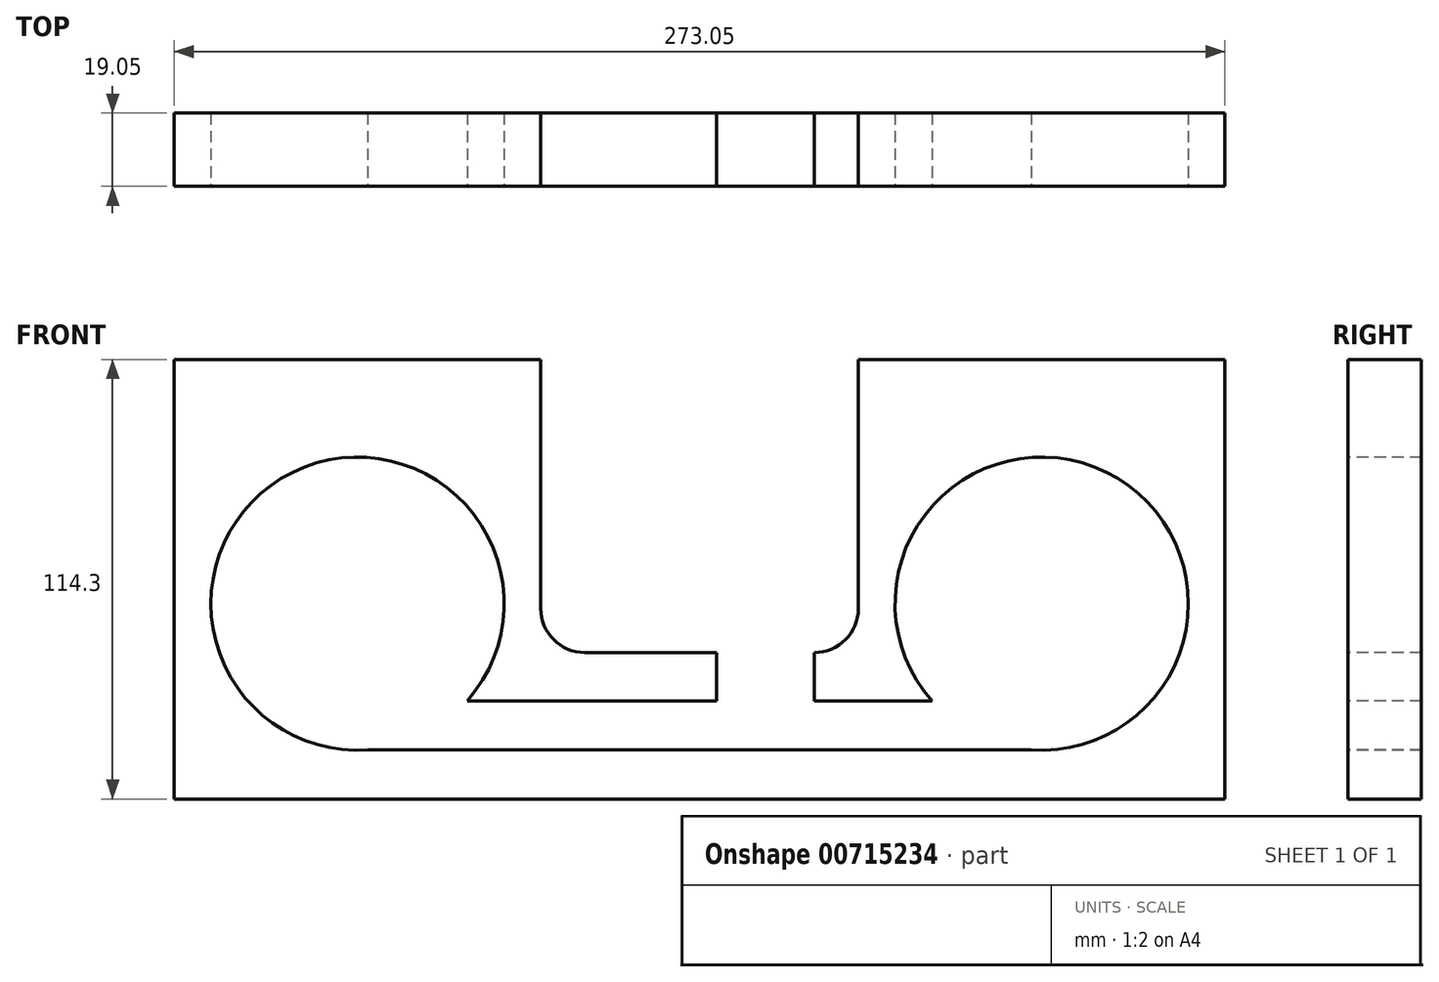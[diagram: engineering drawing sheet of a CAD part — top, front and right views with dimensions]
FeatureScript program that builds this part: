
annotation { "Feature Type Name" : "Feature", "Feature Type Description" : "" }
export const myFeature = defineFeature(function(context is Context, id is Id, definition is map)
    precondition{}
    {
        {
            var Q0;
            Q0=qCreatedBy(makeId("Front.planeOp"),FACE);
            var sketch = newSketch(context, id + "F0", { "sketchPlane" : qUnion([Q0])});
            skLineSegment(sketch, "E0.bottom", {"start": v(0, 0) * mm, "end": v(273.05, 0) * mm});
            skLineSegment(sketch, "E0.top", {"start": v(0, 114.3) * mm, "end": v(273.05, 114.3) * mm});
            skLineSegment(sketch, "E0.left", {"start": v(0, 0) * mm, "end": v(0, 114.3) * mm});
            skLineSegment(sketch, "E0.right", {"start": v(273.05, 0) * mm, "end": v(273.05, 114.3) * mm});
            skSolve(sketch);
        }
        {
            var Q0;
            Q0=makeQuery(id+"F0.imprint","IMPRINT",FACE,{"disambiguationData":[TD([[makeQuery(id+"F0.imprint","IMPRINT",EDGE,{"derivedFrom":sQuery(id+"F0.wireOp",EDGE,"E0.bottom")}),1.0]])]});
            extrude(context, id + "F1", {"entities" : qUnion([Q0]), "depth" : 19.05 * mm, "offsetDistance" : 25.4 * mm});
        }
        {
            var Q0;
            Q0=makeQuery(id+"F1.opExtrude","CAP_FACE",FACE,{"disambiguationData":[OSD([sQuery(id+"F0.wireOp",EDGE,"E0.bottom"),sQuery(id+"F0.wireOp",EDGE,"E0.top"),sQuery(id+"F0.wireOp",EDGE,"E0.left"),sQuery(id+"F0.wireOp",EDGE,"E0.right")])],"isStart":false});
            var sketch = newSketch(context, id + "F2", { "sketchPlane" : qUnion([Q0])});
            skCircle(sketch, "E1", {"center": v(47.63, 50.8) * mm, "radius": 38.1 * mm});
            skCircle(sketch, "E2", {"center": v(225.43, 50.8) * mm, "radius": 38.1 * mm});
            skSolve(sketch);
        }
        {
            var Q0;
            Q0=makeQuery(id+"F2.imprint","IMPRINT",FACE,{"disambiguationData":[TD([[makeQuery(id+"F2.imprint","IMPRINT",EDGE,{"derivedFrom":sQuery(id+"F2.wireOp",EDGE,"E2")}),1.0]])]});
            var Q1;
            Q1=makeQuery(id+"F2.imprint","IMPRINT",FACE,{"disambiguationData":[TD([[makeQuery(id+"F2.imprint","IMPRINT",EDGE,{"derivedFrom":sQuery(id+"F2.wireOp",EDGE,"E1")}),1.0]])]});
            extrude(context, id + "F3", {"entities" : qUnion([Q0, Q1]), "operationType" : NewBodyOperationType.REMOVE, "oppositeDirection" : true, "depth" : 25.4 * mm, "offsetDistance" : 25.4 * mm});
        }
        {
            var Q0;
            Q0=makeQuery(id+"F1.opExtrude","CAP_FACE",FACE,{"disambiguationData":[OSD([sQuery(id+"F0.wireOp",EDGE,"E0.bottom"),sQuery(id+"F0.wireOp",EDGE,"E0.top"),sQuery(id+"F0.wireOp",EDGE,"E0.left"),sQuery(id+"F0.wireOp",EDGE,"E0.right")])],"isStart":false});
            var sketch = newSketch(context, id + "F4", { "sketchPlane" : qUnion([Q0])});
            skLineSegment(sketch, "E3", {"start": v(95.25, 114.3) * mm, "end": v(95.25, 49.53) * mm});
            skLineSegment(sketch, "E4", {"start": v(106.68, 38.1) * mm, "end": v(166.37, 38.1) * mm});
            skLineSegment(sketch, "E5", {"start": v(177.8, 49.53) * mm, "end": v(177.8, 114.3) * mm});
            skPoint(sketch, "E6.visualSharp", {"position": v(95.25, 38.1) * mm});
            skArc(sketch, "E6.filletArc", {"start": v(95.25, 49.53) * mm, "mid": v(98.6, 41.45) * mm, "end": v(106.68, 38.1) * mm});
            skPoint(sketch, "E7.visualSharp", {"position": v(177.8, 38.1) * mm});
            skArc(sketch, "E7.filletArc", {"start": v(166.37, 38.1) * mm, "mid": v(174.45, 41.45) * mm, "end": v(177.8, 49.53) * mm});
            skSolve(sketch);
        }
        {
            var Q0;
            Q0 = qSketchRegion(id + "F4", true);
            var Q1;
            {var subQ1=sQuery(id+"F4.wireOp",EDGE,"E3");Q1=makeQuery(id+"F4.imprint","IMPRINT",FACE,{"disambiguationData":[TD([[makeQuery(id+"F4.imprint","IMPRINT",EDGE,{"derivedFrom":subQ1}),1.0]])]});}
            extrude(context, id + "F5", {"entities" : qUnion([Q0, Q1]), "operationType" : NewBodyOperationType.REMOVE, "oppositeDirection" : true, "depth" : 25.4 * mm, "offsetDistance" : 25.4 * mm});
        }
        {
            var Q0;
            Q0=makeQuery(id+"F1.opExtrude","CAP_FACE",FACE,{"disambiguationData":[OSD([sQuery(id+"F0.wireOp",EDGE,"E0.bottom"),sQuery(id+"F0.wireOp",EDGE,"E0.top"),sQuery(id+"F0.wireOp",EDGE,"E0.left"),sQuery(id+"F0.wireOp",EDGE,"E0.right")])],"isStart":false});
            var sketch = newSketch(context, id + "F6", { "sketchPlane" : qUnion([Q0])});
            skLineSegment(sketch, "E8", {"start": v(166.37, 38.1) * mm, "end": v(140.97, 38.1) * mm});
            skLineSegment(sketch, "E9", {"start": v(140.97, 38.1) * mm, "end": v(140.97, 25.5) * mm});
            skLineSegment(sketch, "E10", {"start": v(140.97, 25.5) * mm, "end": v(76.1, 25.5) * mm});
            skLineSegment(sketch, "E11", {"start": v(76.1, 25.5) * mm, "end": v(50.3, 12.8) * mm});
            skLineSegment(sketch, "E12", {"start": v(50.3, 12.8) * mm, "end": v(228.1, 12.8) * mm});
            skLineSegment(sketch, "E13", {"start": v(228.1, 12.8) * mm, "end": v(196.94, 25.5) * mm});
            skLineSegment(sketch, "E14", {"start": v(196.94, 25.5) * mm, "end": v(166.37, 25.5) * mm});
            skLineSegment(sketch, "E15", {"start": v(166.37, 25.5) * mm, "end": v(166.37, 38.1) * mm});
            skSolve(sketch);
        }
        {
            var Q0;
            {var subQ0=sQuery(id+"F6.wireOp",EDGE,"E13");Q0=makeQuery(id+"F6.imprint","IMPRINT",FACE,{"disambiguationData":[TD([[makeQuery(id+"F6.imprint","IMPRINT",EDGE,{"derivedFrom":subQ0}),1.0]])]});}
            var Q1;
            {var subQ0=sQuery(id+"F6.wireOp",EDGE,"E11");Q1=makeQuery(id+"F6.imprint","IMPRINT",FACE,{"disambiguationData":[TD([[makeQuery(id+"F6.imprint","IMPRINT",EDGE,{"derivedFrom":subQ0}),1.0]])]});}
            var Q2;
            Q2=makeQuery(id+"F6.imprint","IMPRINT",FACE,{"disambiguationData":[TD([[makeQuery(id+"F6.imprint","IMPRINT",EDGE,{"derivedFrom":sQuery(id+"F6.wireOp",EDGE,"E8")}),-1.0]])]});
            extrude(context, id + "F7", {"entities" : qUnion([Q0, Q1, Q2]), "operationType" : NewBodyOperationType.REMOVE, "oppositeDirection" : true, "depth" : 25.4 * mm, "offsetDistance" : 25.4 * mm});
        }
    });
